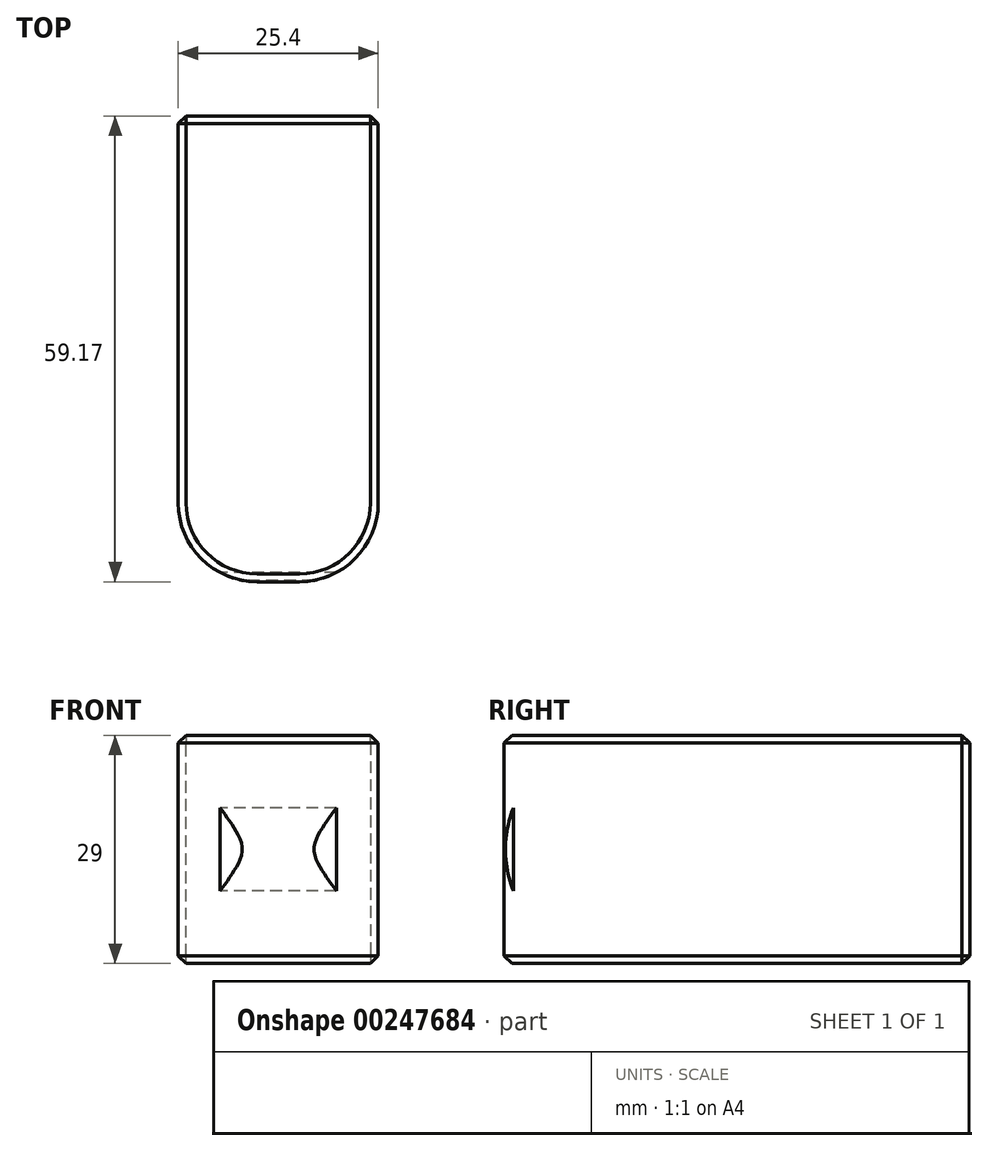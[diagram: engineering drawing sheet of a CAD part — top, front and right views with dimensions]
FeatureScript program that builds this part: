
annotation { "Feature Type Name" : "Feature", "Feature Type Description" : "" }
export const myFeature = defineFeature(function(context is Context, id is Id, definition is map)
    precondition{}
    {
        {
            var Q0;
            Q0=qCreatedBy(makeId("Right.planeOp"),FACE);
            var sketch = newSketch(context, id + "F0", { "sketchPlane" : qUnion([Q0])});
            skLineSegment(sketch, "E0.bottom", {"start": v(-14.23, 16.11) * mm, "end": v(30.27, 16.11) * mm});
            skLineSegment(sketch, "E0.top", {"start": v(-14.23, -12.89) * mm, "end": v(30.27, -12.89) * mm});
            skLineSegment(sketch, "E0.left", {"start": v(-14.23, 16.11) * mm, "end": v(-14.23, -12.89) * mm});
            skLineSegment(sketch, "E0.right", {"start": v(30.27, 16.11) * mm, "end": v(30.27, -12.89) * mm});
            skArc(sketch, "E1", {"start": v(-14.23, 16.11) * mm, "mid": v(-28.73, 1.61) * mm, "end": v(-14.23, -12.89) * mm});
            skLineSegment(sketch, "E2.bottom", {"start": v(-14.23, 16.11) * mm, "end": v(-27.73, 16.11) * mm});
            skLineSegment(sketch, "E2.top", {"start": v(-14.23, -12.89) * mm, "end": v(-27.73, -12.89) * mm});
            skLineSegment(sketch, "E2.right", {"start": v(-27.73, 16.11) * mm, "end": v(-27.73, -12.89) * mm});
            skLineSegment(sketch, "E3.bottom", {"start": v(-14.23, 16.11) * mm, "end": v(-28.9, 16.11) * mm});
            skLineSegment(sketch, "E3.top", {"start": v(-14.23, -12.89) * mm, "end": v(-28.9, -12.89) * mm});
            skLineSegment(sketch, "E3.right", {"start": v(-28.9, 16.11) * mm, "end": v(-28.9, -12.89) * mm});
            skSolve(sketch);
        }
        {
            var Q0;
            {var subQ3=sQuery(id+"F0.wireOp",EDGE,"E3.right");Q0=makeQuery(id+"F0.imprint","IMPRINT",FACE,{"disambiguationData":[TD([[makeQuery(id+"F0.imprint","IMPRINT",EDGE,{"derivedFrom":subQ3}),1.0]])]});}
            var Q1;
            {var subQ0=sQuery(id+"F0.wireOp",EDGE,"E3.bottom");var subQ3=sQuery(id+"F0.wireOp",EDGE,"E2.right");var subQ5=makeQuery(id+"F0.imprint","INTERSECT",VERTEX,{"derivedFrom":[subQ3,subQ0]});Q1=makeQuery(id+"F0.imprint","IMPRINT",FACE,{"disambiguationData":[TD([[makeQuery(id+"F0.imprint","IMPRINT",EDGE,{"disambiguationData":[TD([[subQ5,-1.0]])],"derivedFrom":subQ3}),1.0]])]});}
            var Q2;
            {var subQ0=sQuery(id+"F0.wireOp",EDGE,"E3.top");var subQ3=sQuery(id+"F0.wireOp",EDGE,"E2.right");var subQ5=makeQuery(id+"F0.imprint","INTERSECT",VERTEX,{"derivedFrom":[subQ3,subQ0]});Q2=makeQuery(id+"F0.imprint","IMPRINT",FACE,{"disambiguationData":[TD([[makeQuery(id+"F0.imprint","IMPRINT",EDGE,{"disambiguationData":[TD([[subQ5,1.0]])],"derivedFrom":subQ3}),1.0]])]});}
            var Q3;
            {var subQ0=sQuery(id+"F0.wireOp",EDGE,"E0.left");Q3=makeQuery(id+"F0.imprint","IMPRINT",FACE,{"disambiguationData":[TD([[makeQuery(id+"F0.imprint","IMPRINT",EDGE,{"derivedFrom":subQ0}),-1.0]])]});}
            var Q4;
            {var subQ0=sQuery(id+"F0.wireOp",EDGE,"E2.right");var subQ1=sQuery(id+"F0.wireOp",EDGE,"E1");var subQ2=makeQuery(id+"F0.imprint","INTERSECT",VERTEX,{"disambiguationData":[OD(0.0)],"derivedFrom":[subQ1,subQ0]});Q4=makeQuery(id+"F0.imprint","IMPRINT",FACE,{"disambiguationData":[TD([[makeQuery(id+"F0.imprint","IMPRINT",EDGE,{"disambiguationData":[TD([[subQ2,-1.0]])],"derivedFrom":subQ1}),1.0]])]});}
            var Q5;
            Q5=makeQuery(id+"F0.imprint","IMPRINT",FACE,{"disambiguationData":[TD([[makeQuery(id+"F0.imprint","IMPRINT",EDGE,{"derivedFrom":sQuery(id+"F0.wireOp",EDGE,"E0.bottom")}),-1.0]])]});
            extrude(context, id + "F1", {"entities" : qUnion([Q0, Q1, Q2, Q3, Q4, Q5]), "depth" : 25.4 * mm});
        }
        {
            var Q0;
            Q0=makeQuery(id+"F1.opExtrude","CAP_EDGE",EDGE,{"disambiguationData":[OSD([sQuery(id+"F0.wireOp",EDGE,"E3.right")])],"isStart":false});
            var Q1;
            Q1=makeQuery(id+"F1.opExtrude","CAP_EDGE",EDGE,{"disambiguationData":[OSD([sQuery(id+"F0.wireOp",EDGE,"E3.right")])],"isStart":true});
            fillet(context, id + "F2", {"entities" : qUnion([Q0, Q1]), "radius" : 10 * mm, "tangentPropagation" : true, "allowEdgeOverflow" : false});
        }
        {
            var Q0;
            Q0=makeQuery(id+"F1.opExtrude","CAP_EDGE",EDGE,{"disambiguationData":[OSD([sQuery(id+"F0.wireOp",EDGE,"E0.bottom"),sQuery(id+"F0.wireOp",EDGE,"E3.bottom")])],"isStart":false});
            var Q1;
            Q1=makeQuery(id+"F1.opExtrude","CAP_EDGE",EDGE,{"disambiguationData":[OSD([sQuery(id+"F0.wireOp",EDGE,"E0.top"),sQuery(id+"F0.wireOp",EDGE,"E3.top")])],"isStart":false});
            var Q2;
            Q2=makeQuery(id+"F1.opExtrude","SWEPT_EDGE",EDGE,{"disambiguationData":[OSD([sQuery(id+"F0.wireOp",EDGE,"E0.bottom"),sQuery(id+"F0.wireOp",EDGE,"E0.right")])]});
            var Q3;
            Q3=makeQuery(id+"F1.opExtrude","SWEPT_EDGE",EDGE,{"disambiguationData":[OSD([sQuery(id+"F0.wireOp",EDGE,"E0.top"),sQuery(id+"F0.wireOp",EDGE,"E0.right")])]});
            var Q4;
            Q4=makeQuery(id+"F1.opExtrude","CAP_EDGE",EDGE,{"disambiguationData":[OSD([sQuery(id+"F0.wireOp",EDGE,"E0.right")])],"isStart":false});
            var Q5;
            Q5=makeQuery(id+"F1.opExtrude","CAP_EDGE",EDGE,{"disambiguationData":[OSD([sQuery(id+"F0.wireOp",EDGE,"E0.right")])],"isStart":true});
            chamfer(context, id + "F3", {"entities" : qUnion([Q0, Q1, Q2, Q3, Q4, Q5]), "width" : 1 * mm, "tangentPropagation" : true});
        }
    });
